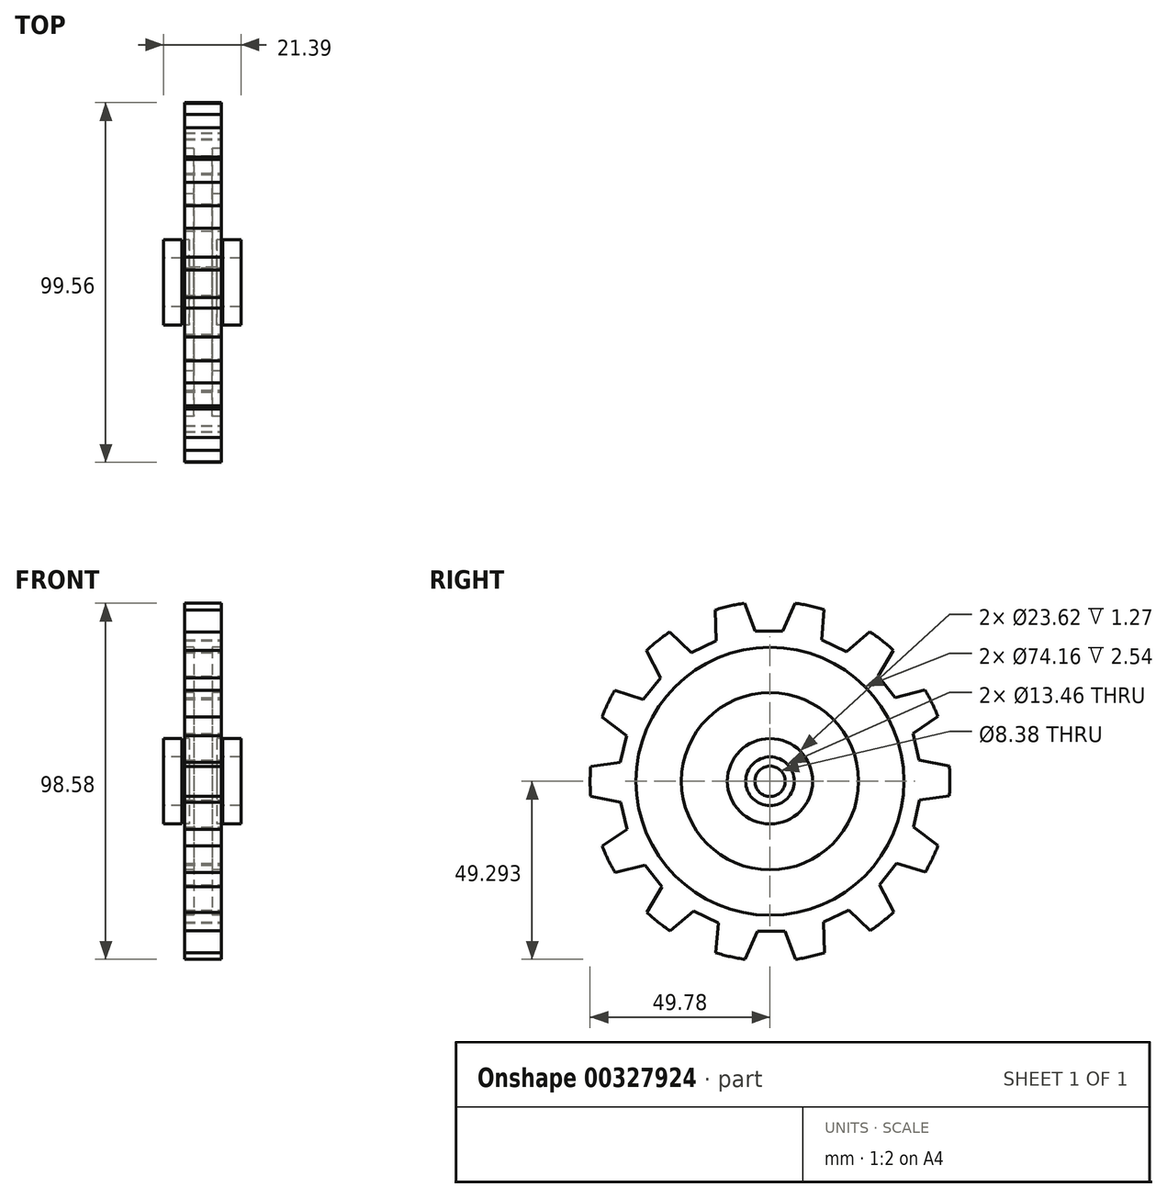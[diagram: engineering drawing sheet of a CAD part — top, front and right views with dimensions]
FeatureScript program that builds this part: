
annotation { "Feature Type Name" : "Feature", "Feature Type Description" : "" }
export const myFeature = defineFeature(function(context is Context, id is Id, definition is map)
    precondition{}
    {
        {
            var Q0;
            Q0=qCreatedBy(makeId("Front.planeOp"),FACE);
            var sketch = newSketch(context, id + "F0", { "sketchPlane" : qUnion([Q0])});
            skLineSegment(sketch, "E0.left", {"start": v(-9.61, 23.98) * mm, "end": v(-9.61, 23.98) * mm});
            skLineSegment(sketch, "E0.right", {"start": v(-3.32, 23.98) * mm, "end": v(-3.32, 23.98) * mm});
            skPoint(sketch, "E1.bottom.start.orphan", {"position": v(-9.97, -4.27) * mm});
            skPoint(sketch, "E2.trimOffspring.start.orphan", {"position": v(3.2, -4.27) * mm});
            skLineSegment(sketch, "E3.bottom", {"start": v(-5.08, 18.87) * mm, "end": v(5.08, 18.87) * mm});
            skLineSegment(sketch, "E3.top", {"start": v(-5.08, 6.17) * mm, "end": v(-2.54, 6.17) * mm});
            skLineSegment(sketch, "E3.left", {"start": v(-5.08, 18.87) * mm, "end": v(-5.08, 6.17) * mm});
            skLineSegment(sketch, "E3.right", {"start": v(5.08, 18.87) * mm, "end": v(5.08, 6.17) * mm});
            skLineSegment(sketch, "E4.left", {"start": v(-2.54, 6.17) * mm, "end": v(-2.54, -6.53) * mm});
            skLineSegment(sketch, "E4.right", {"start": v(2.54, 6.17) * mm, "end": v(2.54, -6.53) * mm});
            skLineSegment(sketch, "E5.bottom", {"start": v(5.08, -6.4) * mm, "end": v(2.54, -6.4) * mm});
            skLineSegment(sketch, "E5.top", {"start": v(10.53, -19.1) * mm, "end": v(5.08, -19.1) * mm});
            skLineSegment(sketch, "E5.left", {"start": v(5.08, -6.4) * mm, "end": v(5.08, -19.1) * mm});
            skLineSegment(sketch, "E5.right", {"start": v(-5.08, -6.4) * mm, "end": v(-5.08, -19.1) * mm});
            skPoint(sketch, "E5.middle", {"position": v(0, -12.75) * mm});
            skLineSegment(sketch, "E6.bottom", {"start": v(-10.51, -19.1) * mm, "end": v(-12, -19.1) * mm});
            skPoint(sketch, "E6.middle", {"position": v(-8.15, -19.1) * mm});
            skLineSegment(sketch, "E7.top", {"start": v(10.53, -24.18) * mm, "end": v(5.45, -24.18) * mm});
            skLineSegment(sketch, "E7.left", {"start": v(10.53, -19.1) * mm, "end": v(10.53, -24.18) * mm});
            skLineSegment(sketch, "E7.right", {"start": v(5.45, -19.1) * mm, "end": v(5.45, -24.18) * mm});
            skPoint(sketch, "E7.middle", {"position": v(8, -21.64) * mm});
            skLineSegment(sketch, "E8.bottom", {"start": v(3.8, -19.1) * mm, "end": v(-3.81, -19.1) * mm});
            skLineSegment(sketch, "E8.top", {"start": v(3.8, -26.72) * mm, "end": v(-3.81, -26.72) * mm});
            skLineSegment(sketch, "E8.left", {"start": v(3.8, -19.1) * mm, "end": v(3.8, -26.72) * mm});
            skLineSegment(sketch, "E8.right", {"start": v(-3.81, -19.1) * mm, "end": v(-3.81, -26.72) * mm});
            skPoint(sketch, "E8.middle", {"position": v(0, -22.9) * mm});
            skPoint(sketch, "E6.top.start.orphan", {"position": v(-4.3, -19.1) * mm});
            skPoint(sketch, "E6.right.end.orphan", {"position": v(-5.78, -19.1) * mm});
            skLineSegment(sketch, "E9.top", {"start": v(-5.78, -24.18) * mm, "end": v(-10.86, -24.18) * mm});
            skLineSegment(sketch, "E9.left", {"start": v(-5.78, -19.1) * mm, "end": v(-5.78, -24.18) * mm});
            skLineSegment(sketch, "E9.right", {"start": v(-10.86, -19.1) * mm, "end": v(-10.86, -24.18) * mm});
            skPoint(sketch, "E9.middle", {"position": v(-8.32, -21.64) * mm});
            skLineSegment(sketch, "E10.trimOffspring", {"start": v(2.54, 6.17) * mm, "end": v(5.08, 6.17) * mm});
            skLineSegment(sketch, "E11.trimOffspring", {"start": v(-2.54, -6.4) * mm, "end": v(-5.08, -6.4) * mm});
            skLineSegment(sketch, "E12.trimOffspring", {"start": v(5.45, -19.1) * mm, "end": v(-5.78, -19.1) * mm});
            skLineSegment(sketch, "E13.trimOffspring", {"start": v(-10.51, -19.1) * mm, "end": v(-10.86, -19.1) * mm});
            skLineSegment(sketch, "E14.trimOffspring", {"start": v(-5.08, -19.1) * mm, "end": v(-10.51, -19.1) * mm});
            skPoint(sketch, "E15.start.orphan", {"position": v(0, -30.86) * mm});
            skLineSegment(sketch, "E16", {"start": v(-12.3, -30.9) * mm, "end": v(13.13, -30.9) * mm, "construction": true});
            skSolve(sketch);
        }
        {
            var Q0;
            Q0 = qSketchRegion(id + "F0", true);
            var Q1;
            Q1=sQuery(id+"F0.wireOp",EDGE,"E16");
            revolve(context, id + "F1", {"surfaceOperationType" : NewSurfaceOperationType.NEW, "entities" : qUnion([Q0]), "axis" : qUnion([Q1]), "revolveType" : RevolveType.FULL});
        }
        {
            var Q0;
            Q0=qCreatedBy(makeId("Right.planeOp"),FACE);
            var sketch = newSketch(context, id + "F2", { "sketchPlane" : qUnion([Q0])});
            skLineSegment(sketch, "E17", {"start": v(-4.13, 10.62) * mm, "end": v(3.5, 10.62) * mm});
            skLineSegment(sketch, "E18", {"start": v(-4.13, 10.62) * mm, "end": v(-7.32, 18.95) * mm});
            skLineSegment(sketch, "E19", {"start": v(3.5, 10.62) * mm, "end": v(7.21, 18.95) * mm});
            skLineSegment(sketch, "E20", {"start": v(-7.32, 18.95) * mm, "end": v(7.21, 18.95) * mm});
            skLineSegment(sketch, "E21.bottom", {"start": v(7.21, 18.95) * mm, "end": v(-7.21, 18.95) * mm});
            skLineSegment(sketch, "E21.top", {"start": v(7.21, 27.11) * mm, "end": v(-7.21, 27.11) * mm});
            skLineSegment(sketch, "E21.left", {"start": v(7.21, 18.95) * mm, "end": v(7.21, 27.11) * mm});
            skLineSegment(sketch, "E21.right", {"start": v(-7.21, 18.95) * mm, "end": v(-7.21, 27.11) * mm});
            skPoint(sketch, "E21.middle", {"position": v(0, 23.03) * mm});
            skSolve(sketch);
        }
        {
            var Q0;
            Q0=makeQuery(id+"F2.imprint","IMPRINT",FACE,{"disambiguationData":[TD([[makeQuery(id+"F2.imprint","IMPRINT",EDGE,{"derivedFrom":sQuery(id+"F2.wireOp",EDGE,"E17")}),1.0]])]});
            extrude(context, id + "F3", {"entities" : qUnion([Q0]), "operationType" : NewBodyOperationType.REMOVE, "endBound" : BoundingType.SYMMETRIC, "oppositeDirection" : true, "depth" : 25.4 * mm});
        }
        {
            var Q0;
            Q0=makeQuery(id+"F3.boolean.opBoolean","COPY",FACE,{"derivedFrom":makeQuery(id+"F3.opExtrude","SWEPT_FACE",FACE,{"disambiguationData":[OSD([sQuery(id+"F2.wireOp",EDGE,"E17")])]})});
            var Q1;
            Q1=makeQuery(id+"F3.boolean.opBoolean","COPY",FACE,{"derivedFrom":makeQuery(id+"F3.opExtrude","SWEPT_FACE",FACE,{"disambiguationData":[OSD([sQuery(id+"F2.wireOp",EDGE,"E18")])]})});
            var Q2;
            Q2=makeQuery(id+"F3.boolean.opBoolean","COPY",FACE,{"derivedFrom":makeQuery(id+"F3.opExtrude","SWEPT_FACE",FACE,{"disambiguationData":[OSD([sQuery(id+"F2.wireOp",EDGE,"E19")])]})});
            var Q3;
            Q3=makeQuery(id+"F1.opRevolve","SWEPT_EDGE",EDGE,{"disambiguationData":[OSD([sQuery(id+"F0.wireOp",EDGE,"E3.right"),sQuery(id+"F0.wireOp",EDGE,"E10.trimOffspring")])]});
            circularPattern(context, id + "F4", {"patternType" : PatternType.FACE, "faces" : qUnion([Q0, Q1, Q2]), "axis" : qUnion([Q3]), "angle" : 360 * degree, "instanceCount" : 28, "equalSpace" : true, "isCentered" : true});
        }
    });
